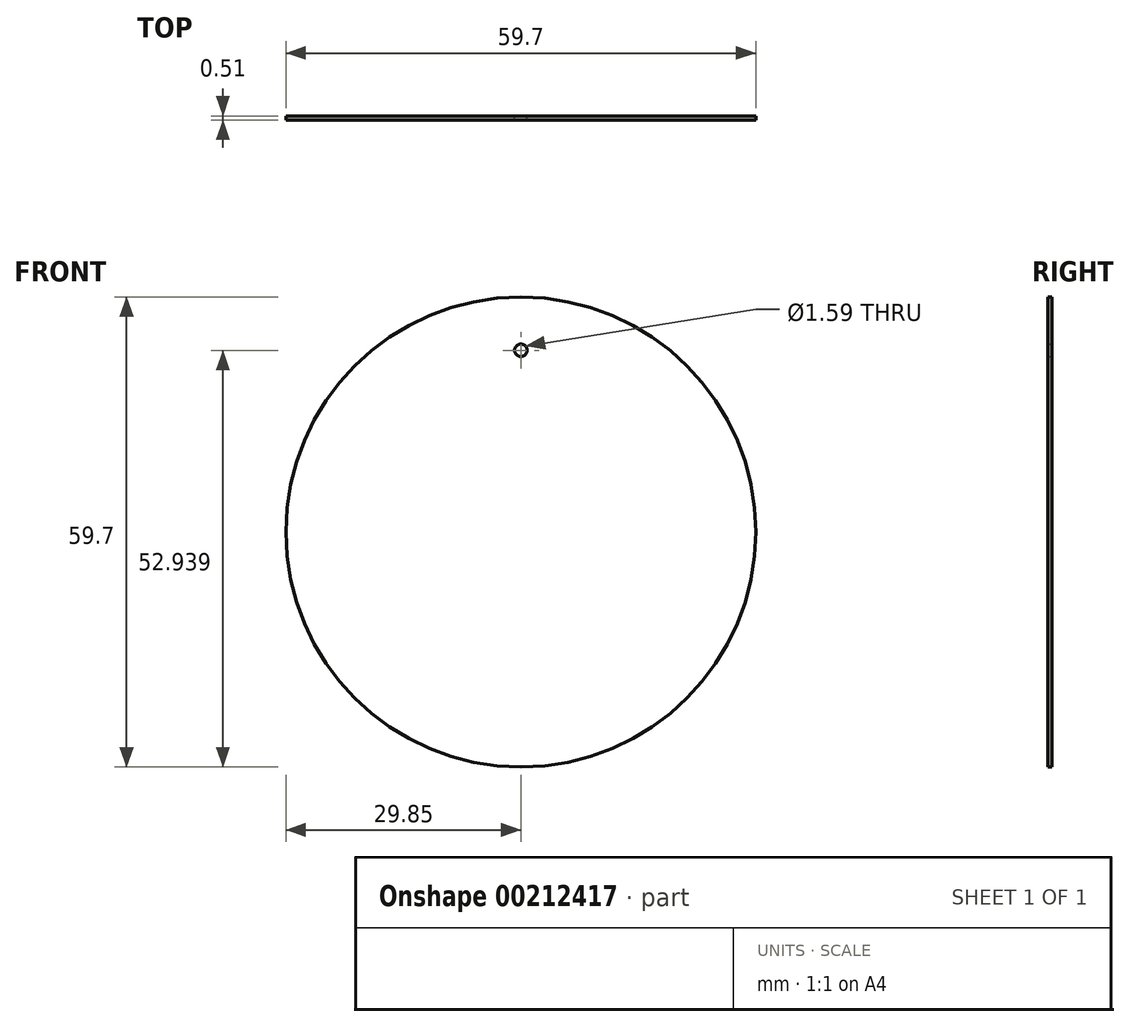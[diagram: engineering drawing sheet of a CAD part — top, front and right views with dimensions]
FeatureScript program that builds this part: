
annotation { "Feature Type Name" : "Feature", "Feature Type Description" : "" }
export const myFeature = defineFeature(function(context is Context, id is Id, definition is map)
    precondition{}
    {
        {
            var Q0;
            Q0=qCreatedBy(makeId("Front.planeOp"),FACE);
            var sketch = newSketch(context, id + "F0", { "sketchPlane" : qUnion([Q0])});
            skCircle(sketch, "E0", {"center": v(0, 0) * mm, "radius": 29.85 * mm});
            skLineSegment(sketch, "E1", {"start": v(0, 0) * mm, "end": v(0, 23.09) * mm, "construction": true});
            skSolve(sketch);
        }
        {
            var Q0;
            Q0 = qSketchRegion(id + "F0", true);
            extrude(context, id + "F1", {"entities" : qUnion([Q0]), "depth" : 0.5 * mm});
        }
        {
            var Q0;
            Q0=sQuery(id+"F0.wireOp",VERTEX,"E1.end");
            var Q1;
            Q1=makeQuery(id+"F1.opExtrude","SWEPT_BODY",BODY,{"disambiguationData":[OSD([sQuery(id+"F0.wireOp",EDGE,"E0")])]});
            hole(context, id + "F2", {"style" : HoleStyle.SIMPLE, "endStyle" : HoleEndStyle.THROUGH, "oppositeDirection" : true, "holeDiameter" : 1.59 * mm, "locations" : qUnion([Q0]), "scope" : qUnion([Q1]), "isTappedThrough" : true});
        }
    });
